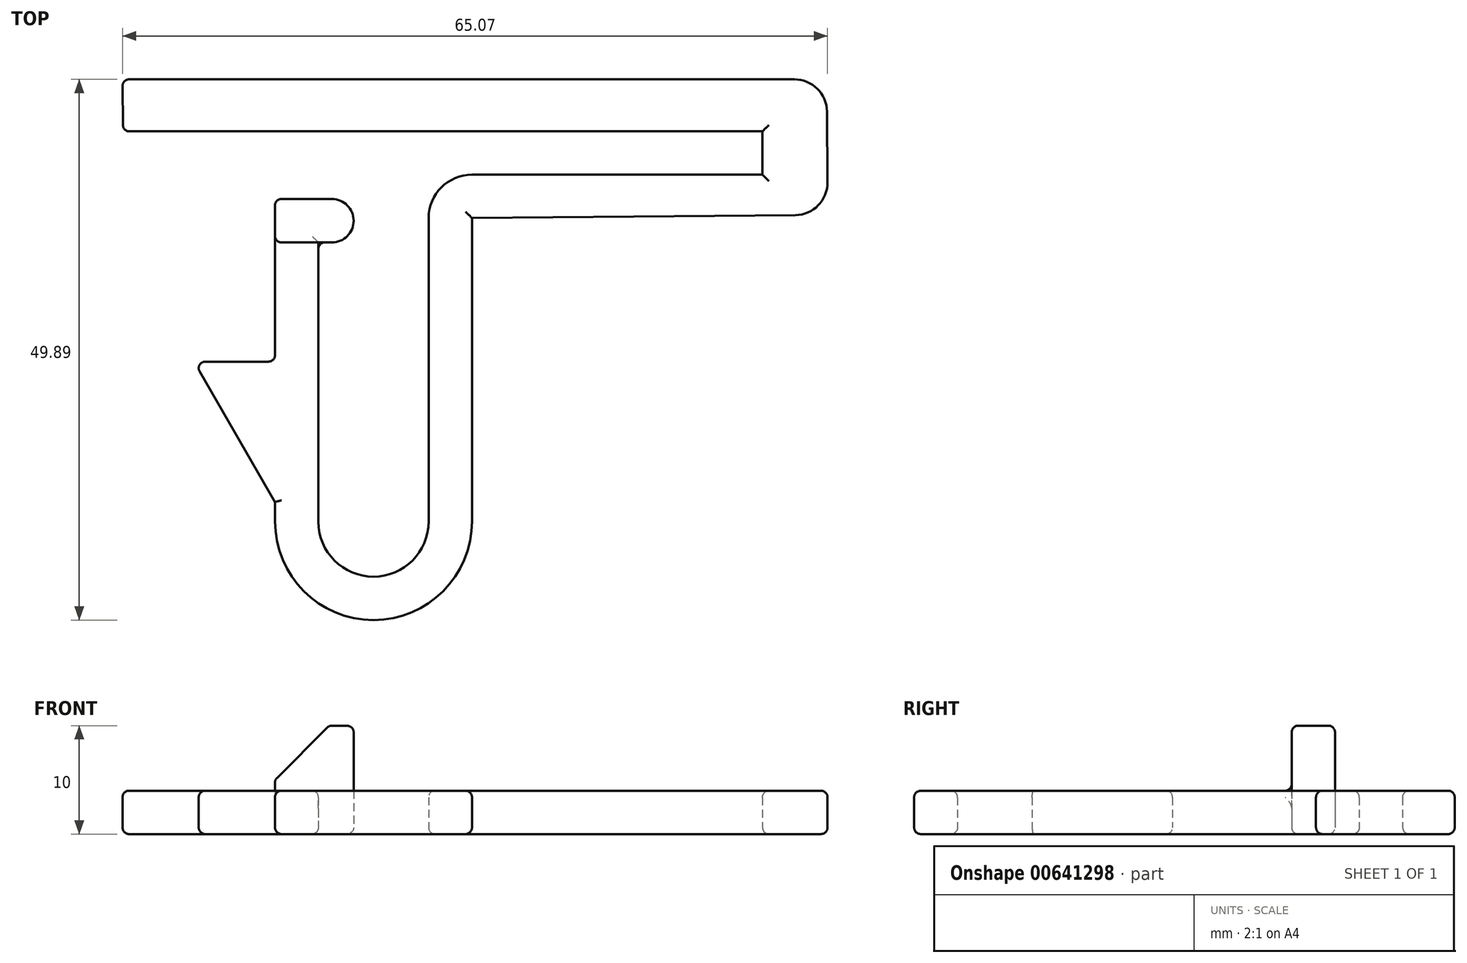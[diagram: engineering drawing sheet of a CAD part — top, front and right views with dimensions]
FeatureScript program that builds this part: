
annotation { "Feature Type Name" : "Feature", "Feature Type Description" : "" }
export const myFeature = defineFeature(function(context is Context, id is Id, definition is map)
    precondition{}
    {
        {
            var Q0;
            Q0=qCreatedBy(makeId("Top.planeOp"),FACE);
            var sketch = newSketch(context, id + "F0", { "sketchPlane" : qUnion([Q0])});
            skLineSegment(sketch, "E0.bottom", {"start": v(-68.37, 12.8) * mm, "end": v(-6.35, 12.8) * mm});
            skLineSegment(sketch, "E0.left", {"start": v(-68.37, 12.8) * mm, "end": v(-68.33, 8) * mm});
            skLineSegment(sketch, "E0.right", {"start": v(-3.35, 9.82) * mm, "end": v(-3.3, 3.3) * mm});
            skLineSegment(sketch, "E1", {"start": v(-54.3, -26.2) * mm, "end": v(-61.78, -13.25) * mm});
            skLineSegment(sketch, "E2", {"start": v(-61.78, -13.25) * mm, "end": v(-54.3, -13.25) * mm});
            skLineSegment(sketch, "E3", {"start": v(-54.3, -13.25) * mm, "end": v(-54.3, 1.75) * mm});
            skLineSegment(sketch, "E4", {"start": v(-9.3, 4) * mm, "end": v(-9.3, 8) * mm});
            skLineSegment(sketch, "E5", {"start": v(-9.3, 8) * mm, "end": v(-68.33, 8) * mm});
            skPoint(sketch, "E6.visualSharp", {"position": v(-3.37, 12.8) * mm});
            skArc(sketch, "E6.filletArc", {"start": v(-3.35, 9.82) * mm, "mid": v(-4.24, 11.93) * mm, "end": v(-6.35, 12.8) * mm});
            skPoint(sketch, "E7.visualSharp", {"position": v(-3.28, 0.3) * mm});
            skArc(sketch, "E7.filletArc", {"start": v(-6.27, 0.28) * mm, "mid": v(-4.16, 1.17) * mm, "end": v(-3.3, 3.3) * mm});
            skLineSegment(sketch, "E8", {"start": v(-9.3, 4) * mm, "end": v(-36.12, 4) * mm});
            skLineSegment(sketch, "E9", {"start": v(-6.27, 0.28) * mm, "end": v(-36.12, 0) * mm});
            skLineSegment(sketch, "E10", {"start": v(-54.3, -26.2) * mm, "end": v(-54.3, -28) * mm});
            skLineSegment(sketch, "E11", {"start": v(-36.12, 0) * mm, "end": v(-36.12, -28) * mm});
            skLineSegment(sketch, "E12", {"start": v(-40.12, 0) * mm, "end": v(-40.12, -28) * mm});
            skArc(sketch, "E13", {"start": v(-36.12, 4) * mm, "mid": v(-38.95, 2.83) * mm, "end": v(-40.12, 0) * mm});
            skArc(sketch, "E14", {"start": v(-54.3, -28) * mm, "mid": v(-45.2, -37.09) * mm, "end": v(-36.12, -28) * mm});
            skLineSegment(sketch, "E15", {"start": v(-50.3, 1.75) * mm, "end": v(-50.3, -28) * mm});
            skArc(sketch, "E16", {"start": v(-40.12, -28) * mm, "mid": v(-45.2, -33.09) * mm, "end": v(-50.3, -28) * mm});
            skLineSegment(sketch, "E17", {"start": v(-50.3, 1.75) * mm, "end": v(-54.3, 1.75) * mm});
            skSolve(sketch);
        }
        {
            var Q0;
            Q0=makeQuery(id+"F0.imprint","IMPRINT",FACE,{"disambiguationData":[TD([[makeQuery(id+"F0.imprint","IMPRINT",EDGE,{"derivedFrom":sQuery(id+"F0.wireOp",EDGE,"E0.bottom")}),-1.0]])]});
            extrude(context, id + "F1", {"entities" : qUnion([Q0]), "depth" : 4 * mm, "offsetDistance" : 25 * mm});
        }
        {
            var Q0;
            Q0=makeQuery(id+"F1.opExtrude","CAP_FACE",FACE,{"disambiguationData":[OSD([sQuery(id+"F0.wireOp",EDGE,"E0.bottom"),sQuery(id+"F0.wireOp",EDGE,"E0.left"),sQuery(id+"F0.wireOp",EDGE,"E0.right"),sQuery(id+"F0.wireOp",EDGE,"E1"),sQuery(id+"F0.wireOp",EDGE,"E2"),sQuery(id+"F0.wireOp",EDGE,"E3"),sQuery(id+"F0.wireOp",EDGE,"E4"),sQuery(id+"F0.wireOp",EDGE,"E5"),sQuery(id+"F0.wireOp",EDGE,"E6.filletArc"),sQuery(id+"F0.wireOp",EDGE,"E7.filletArc"),sQuery(id+"F0.wireOp",EDGE,"E8"),sQuery(id+"F0.wireOp",EDGE,"E9"),sQuery(id+"F0.wireOp",EDGE,"E10"),sQuery(id+"F0.wireOp",EDGE,"E11"),sQuery(id+"F0.wireOp",EDGE,"E12"),sQuery(id+"F0.wireOp",EDGE,"E13"),sQuery(id+"F0.wireOp",EDGE,"E14"),sQuery(id+"F0.wireOp",EDGE,"E15"),sQuery(id+"F0.wireOp",EDGE,"E16"),sQuery(id+"F0.wireOp",EDGE,"E17")])],"isStart":true});
            var sketch = newSketch(context, id + "F2", { "sketchPlane" : qUnion([Q0])});
            skArc(sketch, "E18", {"start": v(-49.04, -1.75) * mm, "mid": v(-47.04, 0.25) * mm, "end": v(-49.04, 2.25) * mm});
            skLineSegment(sketch, "E19", {"start": v(-49.04, 2.25) * mm, "end": v(-54.3, 2.25) * mm});
            skPoint(sketch, "E19.endSnap0", {"position": v(-54.3, 5.75) * mm});
            skLineSegment(sketch, "E20", {"start": v(-54.3, -1.75) * mm, "end": v(-49.04, -1.75) * mm});
            skSolve(sketch);
        }
        {
            var Q0;
            {var subQ0=sQuery(id+"F2.wireOp",EDGE,"E18");Q0=makeQuery(id+"F2.imprint","IMPRINT",FACE,{"disambiguationData":[TD([[makeQuery(id+"F2.imprint","IMPRINT",EDGE,{"derivedFrom":subQ0}),1.0]])]});}
            var Q1;
            {var subQ3=sQuery(id+"F2.wireOp",EDGE,"E19");Q1=makeQuery(id+"F2.imprint","IMPRINT",FACE,{"disambiguationData":[TD([[makeQuery(id+"F2.imprint","IMPRINT",EDGE,{"derivedFrom":subQ3}),1.0]])]});}
            extrude(context, id + "F3", {"entities" : qUnion([Q0, Q1]), "operationType" : NewBodyOperationType.ADD, "oppositeDirection" : true, "depth" : 10 * mm, "offsetDistance" : 25 * mm});
        }
        {
            var Q0;
            Q0=makeQuery(id+"F3.opExtrude","CAP_EDGE",EDGE,{"disambiguationData":[OSD([sQuery(id+"F0.wireOp",EDGE,"E3")])],"isStart":false});
            chamfer(context, id + "F4", {"entities" : qUnion([Q0]), "width" : 5 * mm, "tangentPropagation" : true});
        }
        {
            var Q0;
            Q0=makeQuery(id+"F1.opExtrude","CAP_FACE",FACE,{"disambiguationData":[OSD([sQuery(id+"F0.wireOp",EDGE,"E0.bottom"),sQuery(id+"F0.wireOp",EDGE,"E0.left"),sQuery(id+"F0.wireOp",EDGE,"E0.right"),sQuery(id+"F0.wireOp",EDGE,"E1"),sQuery(id+"F0.wireOp",EDGE,"E2"),sQuery(id+"F0.wireOp",EDGE,"E3"),sQuery(id+"F0.wireOp",EDGE,"E4"),sQuery(id+"F0.wireOp",EDGE,"E5"),sQuery(id+"F0.wireOp",EDGE,"E6.filletArc"),sQuery(id+"F0.wireOp",EDGE,"E7.filletArc"),sQuery(id+"F0.wireOp",EDGE,"E8"),sQuery(id+"F0.wireOp",EDGE,"E9"),sQuery(id+"F0.wireOp",EDGE,"E10"),sQuery(id+"F0.wireOp",EDGE,"E11"),sQuery(id+"F0.wireOp",EDGE,"E12"),sQuery(id+"F0.wireOp",EDGE,"E13"),sQuery(id+"F0.wireOp",EDGE,"E14"),sQuery(id+"F0.wireOp",EDGE,"E15"),sQuery(id+"F0.wireOp",EDGE,"E16"),sQuery(id+"F0.wireOp",EDGE,"E17")])],"isStart":false});
            var Q1;
            Q1=makeQuery(id+"F1.opExtrude","SWEPT_EDGE",EDGE,{"disambiguationData":[OSD([sQuery(id+"F0.wireOp",EDGE,"E1"),sQuery(id+"F0.wireOp",EDGE,"E2")])]});
            var Q2;
            Q2=makeQuery(id+"F1.opExtrude","SWEPT_EDGE",EDGE,{"disambiguationData":[OSD([sQuery(id+"F0.wireOp",EDGE,"E0.left"),sQuery(id+"F0.wireOp",EDGE,"E5")])]});
            var Q3;
            Q3=makeQuery(id+"F1.opExtrude","SWEPT_EDGE",EDGE,{"disambiguationData":[OSD([sQuery(id+"F0.wireOp",EDGE,"E0.bottom"),sQuery(id+"F0.wireOp",EDGE,"E0.left")])]});
            var Q4;
            {var subQ0=sQuery(id+"F0.wireOp",EDGE,"E3");Q4=makeQuery(id+"F3.boolean.opBoolean","MERGE",EDGE,{"derivedFrom":[makeQuery(id+"F1.opExtrude","SWEPT_EDGE",EDGE,{"disambiguationData":[OSD([subQ0,sQuery(id+"F0.wireOp",EDGE,"E17")])]}),makeQuery(id+"F3.opExtrude","SWEPT_EDGE",EDGE,{"disambiguationData":[OSD([subQ0,sQuery(id+"F2.wireOp",EDGE,"E20")])]})]});}
            var Q5;
            Q5=makeQuery(id+"F4.opChamfer","BLEND_EDGE",EDGE,{"blendedFrom":[makeQuery(id+"F3.opExtrude","CAP_EDGE",EDGE,{"disambiguationData":[OSD([sQuery(id+"F0.wireOp",EDGE,"E3")])],"isStart":false}),makeQuery(id+"F3.boolean.opBoolean","MERGE",FACE,{"derivedFrom":[makeQuery(id+"F1.opExtrude","SWEPT_FACE",FACE,{"disambiguationData":[OSD([sQuery(id+"F0.wireOp",EDGE,"E17")])]}),makeQuery(id+"F3.opExtrude","SWEPT_FACE",FACE,{"disambiguationData":[OSD([sQuery(id+"F2.wireOp",EDGE,"E20")])]})]})],"blendedInto":[makeQuery(id+"F3.boolean.opBoolean","MERGE",FACE,{"derivedFrom":[makeQuery(id+"F1.opExtrude","SWEPT_FACE",FACE,{"disambiguationData":[OSD([sQuery(id+"F0.wireOp",EDGE,"E17")])]}),makeQuery(id+"F3.opExtrude","SWEPT_FACE",FACE,{"disambiguationData":[OSD([sQuery(id+"F2.wireOp",EDGE,"E20")])]})]})]});
            var Q6;
            Q6=makeQuery(id+"F3.opExtrude","CAP_EDGE",EDGE,{"disambiguationData":[OSD([sQuery(id+"F2.wireOp",EDGE,"E18")])],"isStart":false});
            var Q7;
            Q7=makeQuery(id+"F4.opChamfer","BLEND_EDGE",EDGE,{"blendedFrom":[makeQuery(id+"F3.opExtrude","CAP_EDGE",EDGE,{"disambiguationData":[OSD([sQuery(id+"F0.wireOp",EDGE,"E3")])],"isStart":false}),makeQuery(id+"F3.opExtrude","SWEPT_FACE",FACE,{"disambiguationData":[OSD([sQuery(id+"F2.wireOp",EDGE,"E19")])]})],"blendedInto":[makeQuery(id+"F3.opExtrude","SWEPT_FACE",FACE,{"disambiguationData":[OSD([sQuery(id+"F2.wireOp",EDGE,"E19")])]})]});
            var Q8;
            {var subQ0=sQuery(id+"F0.wireOp",EDGE,"E3");Q8=makeQuery(id+"F3.boolean.opBoolean","MERGE",FACE,{"derivedFrom":[makeQuery(id+"F1.opExtrude","CAP_FACE",FACE,{"disambiguationData":[OSD([sQuery(id+"F0.wireOp",EDGE,"E0.bottom"),sQuery(id+"F0.wireOp",EDGE,"E0.left"),sQuery(id+"F0.wireOp",EDGE,"E0.right"),sQuery(id+"F0.wireOp",EDGE,"E1"),sQuery(id+"F0.wireOp",EDGE,"E2"),subQ0,sQuery(id+"F0.wireOp",EDGE,"E4"),sQuery(id+"F0.wireOp",EDGE,"E5"),sQuery(id+"F0.wireOp",EDGE,"E6.filletArc"),sQuery(id+"F0.wireOp",EDGE,"E7.filletArc"),sQuery(id+"F0.wireOp",EDGE,"E8"),sQuery(id+"F0.wireOp",EDGE,"E9"),sQuery(id+"F0.wireOp",EDGE,"E10"),sQuery(id+"F0.wireOp",EDGE,"E11"),sQuery(id+"F0.wireOp",EDGE,"E12"),sQuery(id+"F0.wireOp",EDGE,"E13"),sQuery(id+"F0.wireOp",EDGE,"E14"),sQuery(id+"F0.wireOp",EDGE,"E15"),sQuery(id+"F0.wireOp",EDGE,"E16"),sQuery(id+"F0.wireOp",EDGE,"E17")])],"isStart":true}),makeQuery(id+"F3.opExtrude","CAP_FACE",FACE,{"disambiguationData":[OSD([subQ0,sQuery(id+"F2.wireOp",EDGE,"E18"),sQuery(id+"F2.wireOp",EDGE,"E19"),sQuery(id+"F2.wireOp",EDGE,"E20")])],"isStart":true})]});}
            var Q9;
            {var subQ0=sQuery(id+"F0.wireOp",EDGE,"E3");Q9=makeQuery(id+"F4.opChamfer","BLEND_EDGE",EDGE,{"blendedFrom":[makeQuery(id+"F3.opExtrude","CAP_EDGE",EDGE,{"disambiguationData":[OSD([subQ0])],"isStart":false}),makeQuery(id+"F3.opExtrude","CAP_FACE",FACE,{"disambiguationData":[OSD([subQ0,sQuery(id+"F2.wireOp",EDGE,"E18"),sQuery(id+"F2.wireOp",EDGE,"E19"),sQuery(id+"F2.wireOp",EDGE,"E20")])],"isStart":false})],"blendedInto":[makeQuery(id+"F3.opExtrude","CAP_FACE",FACE,{"disambiguationData":[OSD([subQ0,sQuery(id+"F2.wireOp",EDGE,"E18"),sQuery(id+"F2.wireOp",EDGE,"E19"),sQuery(id+"F2.wireOp",EDGE,"E20")])],"isStart":false})]});}
            var Q10;
            {var subQ0=sQuery(id+"F0.wireOp",EDGE,"E3");Q10=makeQuery(id+"F3.boolean.opBoolean","MERGE",FACE,{"derivedFrom":[makeQuery(id+"F1.opExtrude","SWEPT_FACE",FACE,{"disambiguationData":[OSD([subQ0])]}),makeQuery(id+"F3.opExtrude","SWEPT_FACE",FACE,{"disambiguationData":[OSD([subQ0])]})]});}
            fillet(context, id + "F5", {"entities" : qUnion([Q0, Q1, Q2, Q3, Q4, Q5, Q6, Q7, Q8, Q9, Q10]), "radius" : .6 * mm, "tangentPropagation" : true, "allowEdgeOverflow" : false});
        }
    });
